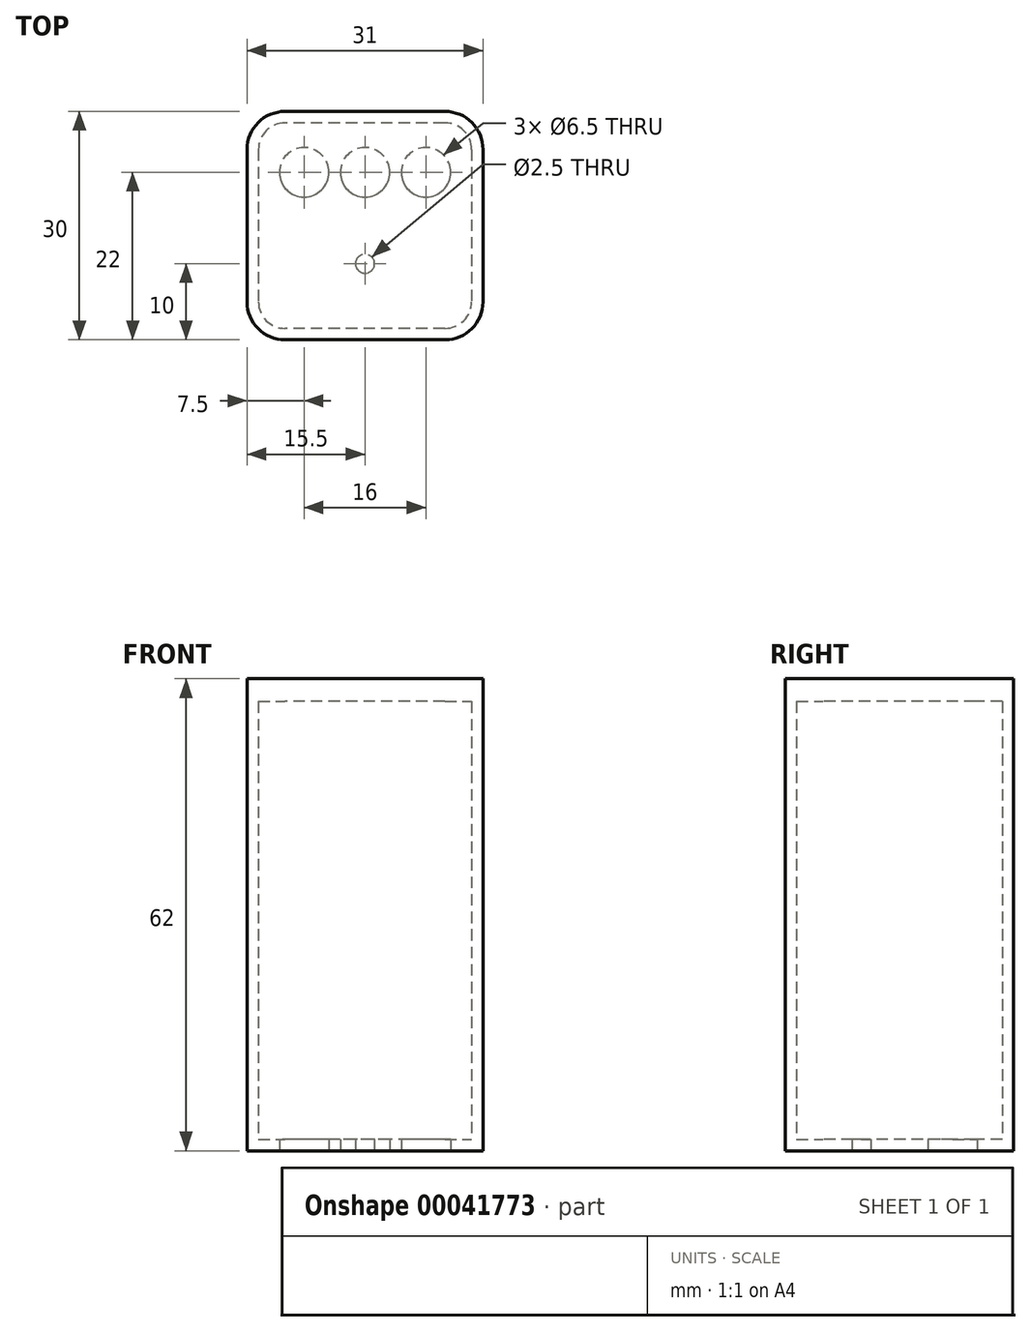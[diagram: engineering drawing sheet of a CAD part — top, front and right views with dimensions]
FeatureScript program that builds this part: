
annotation { "Feature Type Name" : "Feature", "Feature Type Description" : "" }
export const myFeature = defineFeature(function(context is Context, id is Id, definition is map)
    precondition{}
    {
        {
            var Q0;
            Q0=qCreatedBy(makeId("Top.planeOp"),FACE);
            var sketch = newSketch(context, id + "F0", { "sketchPlane" : qUnion([Q0])});
            skLineSegment(sketch, "E0.rect.bottom", {"start": v(15.5, 15) * mm, "end": v(-15.5, 15) * mm});
            skLineSegment(sketch, "E0.rect.top", {"start": v(15.5, -15) * mm, "end": v(-15.5, -15) * mm});
            skLineSegment(sketch, "E0.rect.left", {"start": v(15.5, 15) * mm, "end": v(15.5, -15) * mm});
            skLineSegment(sketch, "E0.rect.right", {"start": v(-15.5, 15) * mm, "end": v(-15.5, -15) * mm});
            skPoint(sketch, "E0.rect.middle", {"position": v(0, 0) * mm});
            skSolve(sketch);
        }
        {
            var Q0;
            Q0 = qSketchRegion(id + "F0", true);
            extrude(context, id + "F1", {"entities" : qUnion([Q0]), "depth" : 60 * mm});
        }
        {
            var Q0;
            Q0=makeQuery(id+"F1.opExtrude","CAP_FACE",FACE,{"disambiguationData":[OSD([sQuery(id+"F0.wireOp",EDGE,"E0.rect.bottom"),sQuery(id+"F0.wireOp",EDGE,"E0.rect.top"),sQuery(id+"F0.wireOp",EDGE,"E0.rect.left"),sQuery(id+"F0.wireOp",EDGE,"E0.rect.right")])],"isStart":false});
            shell(context, id + "F2", {"entities" : qUnion([Q0]), "thickness" : 1.5 * mm});
        }
        {
            var Q0;
            Q0=makeQuery(id+"F1.opExtrude","CAP_FACE",FACE,{"disambiguationData":[OSD([sQuery(id+"F0.wireOp",EDGE,"E0.rect.bottom"),sQuery(id+"F0.wireOp",EDGE,"E0.rect.top"),sQuery(id+"F0.wireOp",EDGE,"E0.rect.left"),sQuery(id+"F0.wireOp",EDGE,"E0.rect.right")])],"isStart":true});
            var sketch = newSketch(context, id + "F3", { "sketchPlane" : qUnion([Q0])});
            skLineSegment(sketch, "E1", {"start": v(15.5, -7) * mm, "end": v(-15.5, -7) * mm, "construction": true});
            skLineSegment(sketch, "E2", {"start": v(15.5, 5) * mm, "end": v(-15.5, 5) * mm, "construction": true});
            skCircle(sketch, "E3", {"center": v(0, -7) * mm, "radius": 3.25 * mm});
            skCircle(sketch, "E4", {"center": v(-8, -7) * mm, "radius": 3.25 * mm});
            skCircle(sketch, "E5", {"center": v(8, -7) * mm, "radius": 3.25 * mm});
            skCircle(sketch, "E6", {"center": v(0, 5) * mm, "radius": 1.25 * mm});
            skSolve(sketch);
        }
        {
            var Q0;
            Q0 = qSketchRegion(id + "F3", true);
            extrude(context, id + "F4", {"entities" : qUnion([Q0]), "operationType" : NewBodyOperationType.REMOVE, "endBound" : BoundingType.UP_TO_NEXT, "oppositeDirection" : true, "depth" : 25 * mm});
        }
        {
            var Q0;
            Q0=makeQuery(id+"F1.opExtrude","SWEPT_EDGE",EDGE,{"disambiguationData":[OSD([sQuery(id+"F0.wireOp",EDGE,"E0.rect.bottom"),sQuery(id+"F0.wireOp",EDGE,"E0.rect.left")])]});
            var Q1;
            Q1=makeQuery(id+"F1.opExtrude","SWEPT_EDGE",EDGE,{"disambiguationData":[OSD([sQuery(id+"F0.wireOp",EDGE,"E0.rect.bottom"),sQuery(id+"F0.wireOp",EDGE,"E0.rect.right")])]});
            var Q2;
            Q2=makeQuery(id+"F1.opExtrude","SWEPT_EDGE",EDGE,{"disambiguationData":[OSD([sQuery(id+"F0.wireOp",EDGE,"E0.rect.top"),sQuery(id+"F0.wireOp",EDGE,"E0.rect.right")])]});
            var Q3;
            Q3=makeQuery(id+"F1.opExtrude","SWEPT_EDGE",EDGE,{"disambiguationData":[OSD([sQuery(id+"F0.wireOp",EDGE,"E0.rect.top"),sQuery(id+"F0.wireOp",EDGE,"E0.rect.left")])]});
            fillet(context, id + "F5", {"entities" : qUnion([Q0, Q1, Q2, Q3]), "radius" : 5 * mm, "tangentPropagation" : true, "allowEdgeOverflow" : false});
        }
        {
            var Q0;
            Q0=makeQuery(id+"F2.opShell","OFFSET_EDGE",EDGE,{"disambiguationData":[OSD([sQuery(id+"F0.wireOp",EDGE,"E0.rect.bottom"),sQuery(id+"F0.wireOp",EDGE,"E0.rect.left")])]});
            var Q1;
            Q1=makeQuery(id+"F2.opShell","OFFSET_EDGE",EDGE,{"disambiguationData":[OSD([sQuery(id+"F0.wireOp",EDGE,"E0.rect.bottom"),sQuery(id+"F0.wireOp",EDGE,"E0.rect.right")])]});
            var Q2;
            Q2=makeQuery(id+"F2.opShell","OFFSET_EDGE",EDGE,{"disambiguationData":[OSD([sQuery(id+"F0.wireOp",EDGE,"E0.rect.top"),sQuery(id+"F0.wireOp",EDGE,"E0.rect.right")])]});
            var Q3;
            Q3=makeQuery(id+"F2.opShell","OFFSET_EDGE",EDGE,{"disambiguationData":[OSD([sQuery(id+"F0.wireOp",EDGE,"E0.rect.top"),sQuery(id+"F0.wireOp",EDGE,"E0.rect.left")])]});
            fillet(context, id + "F6", {"entities" : qUnion([Q0, Q1, Q2, Q3]), "radius" : 3.5 * mm, "tangentPropagation" : true, "allowEdgeOverflow" : false});
        }
        {
            var Q0;
            Q0=makeQuery(id+"F1.opExtrude","CAP_FACE",FACE,{"disambiguationData":[OSD([sQuery(id+"F0.wireOp",EDGE,"E0.rect.bottom"),sQuery(id+"F0.wireOp",EDGE,"E0.rect.top"),sQuery(id+"F0.wireOp",EDGE,"E0.rect.left"),sQuery(id+"F0.wireOp",EDGE,"E0.rect.right")])],"isStart":false});
            var sketch = newSketch(context, id + "F7", { "sketchPlane" : qUnion([Q0])});
            skArc(sketch, "E7.1", {"start": v(10.5, -15) * mm, "mid": v(14.04, -13.54) * mm, "end": v(15.5, -10) * mm});
            skLineSegment(sketch, "E7.2", {"start": v(15.5, 10) * mm, "end": v(15.5, -10) * mm});
            skArc(sketch, "E7.3", {"start": v(15.5, 10) * mm, "mid": v(14.04, 13.54) * mm, "end": v(10.5, 15) * mm});
            skLineSegment(sketch, "E7.4", {"start": v(10.5, 15) * mm, "end": v(-10.5, 15) * mm});
            skArc(sketch, "E7.5", {"start": v(-10.5, 15) * mm, "mid": v(-14.04, 13.54) * mm, "end": v(-15.5, 10) * mm});
            skLineSegment(sketch, "E7.6", {"start": v(-15.5, 10) * mm, "end": v(-15.5, -10) * mm});
            skArc(sketch, "E7.7", {"start": v(-15.5, -10) * mm, "mid": v(-14.04, -13.54) * mm, "end": v(-10.5, -15) * mm});
            skLineSegment(sketch, "E7.8", {"start": v(10.5, -15) * mm, "end": v(-10.5, -15) * mm});
            skSolve(sketch);
        }
        {
            var Q0;
            Q0=makeQuery(id+"F7.imprint","IMPRINT",FACE,{"disambiguationData":[TD([[makeQuery(id+"F7.imprint","IMPRINT",EDGE,{"derivedFrom":sQuery(id+"F7.wireOp",EDGE,"E7.1")}),1.0]])]});
            cPlane(context, id + "F8", {"entities" : qUnion([Q0]), "cplaneType" : CPlaneType.OFFSET, "offset" : 2 * mm, "width" : 150 * mm, "height" : 150 * mm});
        }
        {
            var Q0;
            Q0=qCreatedBy(id+"F8.planeOp",FACE);
            var sketch = newSketch(context, id + "F9", { "sketchPlane" : qUnion([Q0])});
            skLineSegment(sketch, "E8.0", {"start": v(15.5, 10) * mm, "end": v(15.5, -10) * mm});
            skArc(sketch, "E8.1", {"start": v(10.5, -15) * mm, "mid": v(14.04, -13.54) * mm, "end": v(15.5, -10) * mm});
            skLineSegment(sketch, "E8.2", {"start": v(10.5, -15) * mm, "end": v(-10.5, -15) * mm});
            skArc(sketch, "E8.3", {"start": v(-15.5, -10) * mm, "mid": v(-14.04, -13.54) * mm, "end": v(-10.5, -15) * mm});
            skLineSegment(sketch, "E8.4", {"start": v(-15.5, 10) * mm, "end": v(-15.5, -10) * mm});
            skArc(sketch, "E8.5", {"start": v(-10.5, 15) * mm, "mid": v(-14.04, 13.54) * mm, "end": v(-15.5, 10) * mm});
            skLineSegment(sketch, "E8.6", {"start": v(10.5, 15) * mm, "end": v(-10.5, 15) * mm});
            skArc(sketch, "E8.7", {"start": v(15.5, 10) * mm, "mid": v(14.04, 13.54) * mm, "end": v(10.5, 15) * mm});
            skSolve(sketch);
        }
        {
            var Q0;
            Q0 = qSketchRegion(id + "F9", true);
            extrude(context, id + "F10", {"entities" : qUnion([Q0]), "oppositeDirection" : true, "depth" : 2 * mm});
        }
        {
            var Q0;
            {var subQ3=sQuery(id+"F0.wireOp",EDGE,"E0.rect.bottom");Q0=makeQuery(id+"F7.imprint","IMPRINT",FACE,{"disambiguationData":[TD([[makeQuery(id+"F7.imprint","IMPRINT",EDGE,{"derivedFrom":makeQuery(id+"F2.opShell","OFFSET_EDGE",EDGE,{"disambiguationData":[OSD([subQ3]),TDD([makeQuery(id+"F1.opExtrude","CAP_EDGE",EDGE,{"disambiguationData":[OSD([subQ3])],"isStart":false})])]})}),1.0]])]});}
            var sketch = newSketch(context, id + "F11", { "sketchPlane" : qUnion([Q0])});
            skSolve(sketch);
        }
        {
            var Q0;
            {var subQ3=sQuery(id+"F0.wireOp",EDGE,"E0.rect.bottom");Q0=makeQuery(id+"F11.imprint","IMPRINT",FACE,{"disambiguationData":[TD([[makeQuery(id+"F11.imprint","IMPRINT",EDGE,{"derivedFrom":makeQuery(id+"F7.imprint","IMPRINT",EDGE,{"derivedFrom":makeQuery(id+"F2.opShell","OFFSET_EDGE",EDGE,{"disambiguationData":[OSD([subQ3]),TDD([makeQuery(id+"F1.opExtrude","CAP_EDGE",EDGE,{"disambiguationData":[OSD([subQ3])],"isStart":false})])]})})}),1.0]])]});}
            extrude(context, id + "F12", {"entities" : qUnion([Q0]), "operationType" : NewBodyOperationType.ADD, "oppositeDirection" : true, "depth" : 1 * mm});
        }
    });
